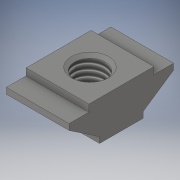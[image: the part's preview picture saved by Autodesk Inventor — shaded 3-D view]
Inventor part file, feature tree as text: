
AUTODESK INVENTOR PART (.ipt)
format: ipt  version: 2019 (Build 230136000, 136)  size: 137,216 bytes
history: native  units: mm
features: other x7, sketch x2, extrude x1, revolve x1, thread x1
ambient origin geometry x8: Origin, YZ Plane, XZ Plane, XY Plane, X Axis, Y Axis, Z Axis, Center Point
bodies: Solid1 (feature_tree)
feature tree (12):
  extrude  "Extrusion1"  TaperAngle=360.0deg  [1 undecoded]
  revolve  "Revolution1"  [1 undecoded]
  thread  "Thread1"  [1 undecoded]
  other  "TIN_4_XY"
  other  "TIN_4_YZ"
  other  "TIN_4_ZX"
  other  "TIN_4_X"
  other  "TIN_4_Y"
  other  "TIN_4_Z"
  other  "TIN_4_Center"
  sketch  "Skizze_1"  dims[d0=13.5mm d1=0.0mm d2=360.0deg]
  sketch  "Skizze_2"  dims[d3=7.147mm d4=0.0mm d5=0.0mm]
note: 3 required parameter values undecoded (feature->parameter linkage not recoverable at this tier; creation-order binding heuristic only, values carry confidence <= 0.55)